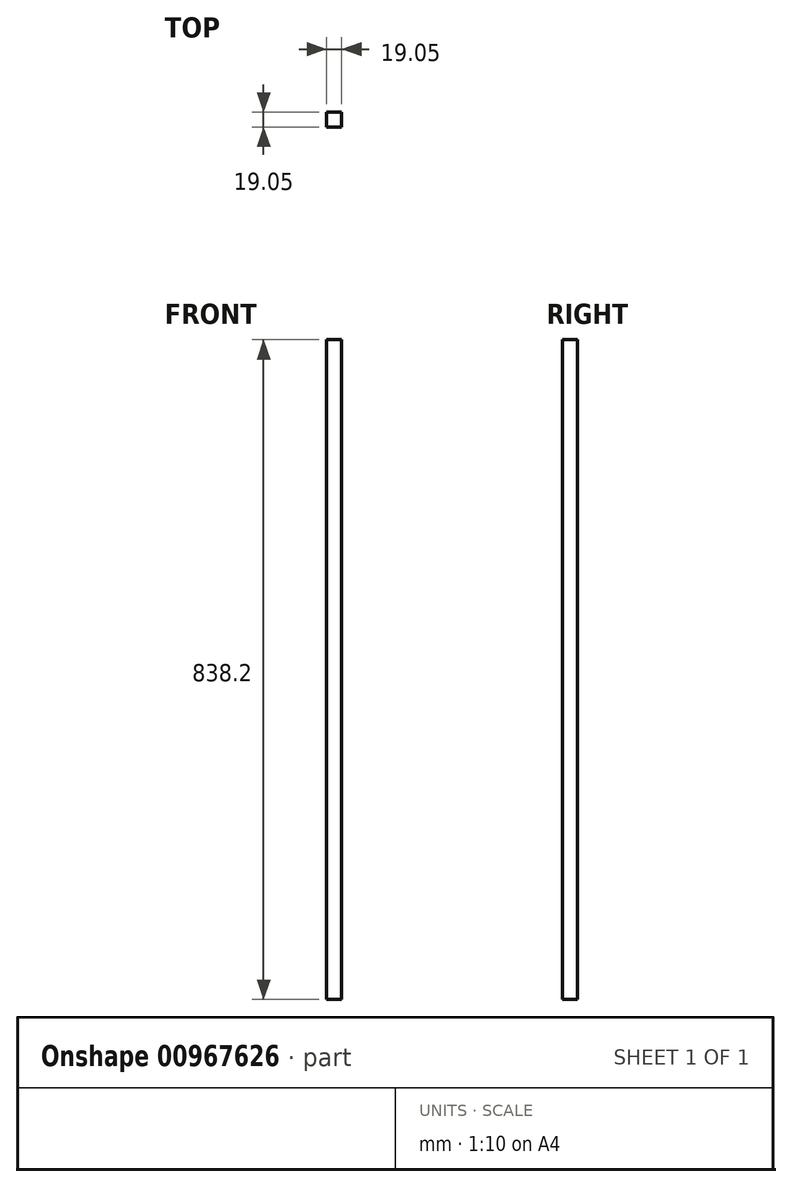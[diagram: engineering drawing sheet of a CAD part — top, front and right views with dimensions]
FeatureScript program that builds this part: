
annotation { "Feature Type Name" : "Feature", "Feature Type Description" : "" }
export const myFeature = defineFeature(function(context is Context, id is Id, definition is map)
    precondition{}
    {
        {
            var Q0;
            Q0=qCreatedBy(makeId("Front.planeOp"),FACE);
            var sketch = newSketch(context, id + "F0", { "sketchPlane" : qUnion([Q0])});
            skLineSegment(sketch, "E0.bottom", {"start": v(0, 0) * mm, "end": v(19.05, 0) * mm});
            skLineSegment(sketch, "E0.top", {"start": v(0, 838.2) * mm, "end": v(19.05, 838.2) * mm});
            skLineSegment(sketch, "E0.left", {"start": v(0, 0) * mm, "end": v(0, 838.2) * mm});
            skLineSegment(sketch, "E0.right", {"start": v(19.05, 0) * mm, "end": v(19.05, 838.2) * mm});
            skSolve(sketch);
        }
        {
            var Q0;
            Q0 = qSketchRegion(id + "F0", true);
            extrude(context, id + "F1", {"entities" : qUnion([Q0]), "depth" : 19.05 * mm, "offsetDistance" : 25.4 * mm});
        }
    });
